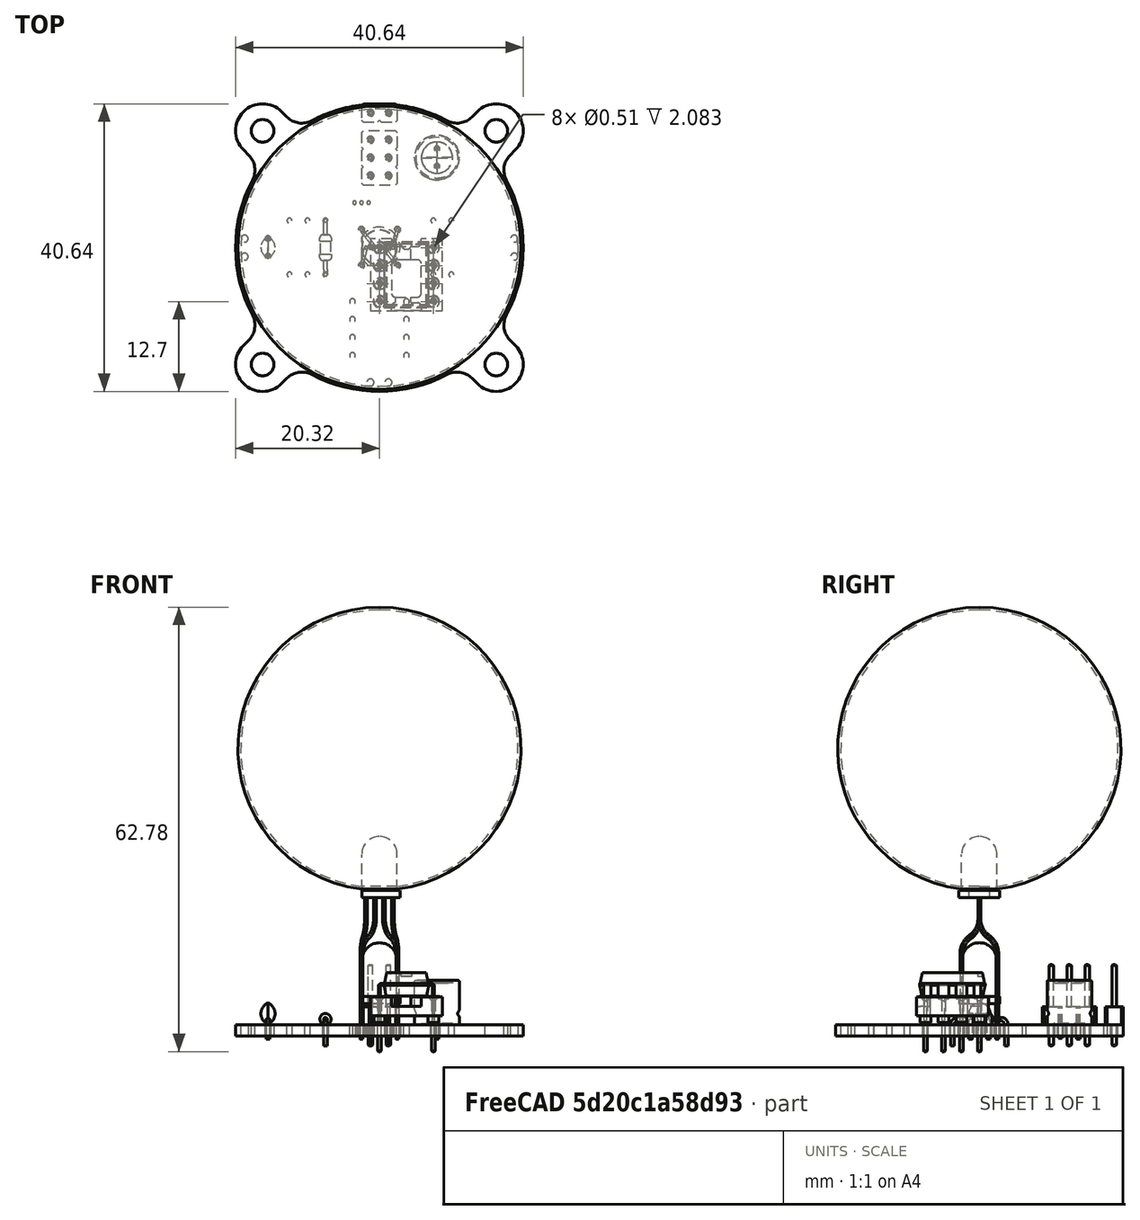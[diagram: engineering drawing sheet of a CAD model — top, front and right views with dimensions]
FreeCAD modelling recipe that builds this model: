
FCSTD DOCUMENT  (FreeCAD 2022.709R28846 (Git))
Label: firefly_v1_grid
License: All rights reserved
LicenseURL: http://en.wikipedia.org/wiki/All_rights_reserved
objects: Part::Feature×21, App::Link×7, App::Part×6, Sketcher::SketchObject×3, Part::FeaturePython×2, PartDesign::CoordinateSystem×1, PartDesign::Revolution×1, PartDesign::Pocket×1, PartDesign::Body×1
note: 32 computed .brp shape members not serialized (recipe doc carries the construction recipe); baked Part::Feature solids carry a one-line shape summary decoded from their .brp

FEATURE [PartDesign::CoordinateSystem] Local_CS_3165
  AttacherType = Attacher::AttachEngine3D
  AttachmentSupport = -> [X_Axis001]
  MapMode = 2
  Support = -> [X_Axis001]
  TreeRank = 0
FEATURE [Part::Feature] Pcb_3165
  Placement = pos=(-50.7999,50.8008,0) rot=(0,0,1;0rad)
  TreeRank = 0
  shape: bbox 40.64 x 40.64 x 1.6 mm, 75 faces (baked)
FEATURE [Sketcher::SketchObject] PCB_Sketch_3165
  ArcFitTolerance = 0
  FullyConstrained = false
  TreeRank = 0
  sketch-geometry (24):
    g0: LineSegment StartX=-19.2041 StartY=13.8159 StartZ=0 EndX=-18.465 EndY=13.0769 EndZ=0
    g1: LineSegment StartX=19.2041 StartY=13.8159 StartZ=0 EndX=18.465 EndY=13.0769 EndZ=0
    g2: LineSegment StartX=-13.0769 StartY=-18.465 StartZ=0 EndX=-13.8159 EndY=-19.2041 EndZ=0
    g3: LineSegment StartX=-18.465 StartY=-13.0769 StartZ=0 EndX=-19.2041 EndY=-13.8159 EndZ=0
    g4: LineSegment StartX=18.465 StartY=-13.0769 StartZ=0 EndX=19.2041 EndY=-13.8159 EndZ=0
    g5: LineSegment StartX=13.0769 StartY=-18.465 StartZ=0 EndX=13.8159 EndY=-19.2041 EndZ=0
    g6: LineSegment StartX=-13.8159 StartY=19.2041 StartZ=0 EndX=-13.0769 EndY=18.465 EndZ=0
    g7: LineSegment StartX=13.8159 StartY=19.2041 StartZ=0 EndX=13.0769 EndY=18.465 EndZ=0
    g8: ArcOfCircle CenterX=16.51 CenterY=-16.51 CenterZ=0 NormalX=0 NormalY=0 NormalZ=-1 AngleXU=2.35619 Radius=3.80999 StartAngle=0 EndAngle=3.14159
    g9: ArcOfCircle CenterX=-16.51 CenterY=-16.51 CenterZ=0 NormalX=0 NormalY=0 NormalZ=-1 AngleXU=-2.35619 Radius=3.80999 StartAngle=0 EndAngle=3.14159
    g10: ArcOfCircle CenterX=-10.9556 CenterY=20.5864 CenterZ=0 NormalX=0 NormalY=0 NormalZ=-1 AngleXU=-2.05985 Radius=3 StartAngle=0 EndAngle=1.27445
    g11: ArcOfCircle CenterX=20.5864 CenterY=10.9556 CenterZ=0 NormalX=0 NormalY=0 NormalZ=-1 AngleXU=-0.489056 Radius=3 StartAngle=0 EndAngle=1.27445
    g12: ArcOfCircle CenterX=-20.5864 CenterY=10.9556 CenterZ=0 NormalX=0 NormalY=0 NormalZ=-1 AngleXU=2.35619 Radius=3 StartAngle=0 EndAngle=1.27445
    g13: ArcOfCircle CenterX=1.9315e-06 CenterY=-1.81384e-07 CenterZ=0 NormalX=0 NormalY=0 NormalZ=-1 AngleXU=-0.489056 Radius=20.32 StartAngle=0 EndAngle=0.978112
    g14: ArcOfCircle CenterX=-20.5864 CenterY=-10.9556 CenterZ=0 NormalX=0 NormalY=0 NormalZ=-1 AngleXU=2.65254 Radius=3 StartAngle=0 EndAngle=1.27445
    g15: ArcOfCircle CenterX=-1.9315e-06 CenterY=-1.81384e-07 CenterZ=0 NormalX=0 NormalY=0 NormalZ=-1 AngleXU=2.65254 Radius=20.32 StartAngle=0 EndAngle=0.978112
    g16: ArcOfCircle CenterX=-16.51 CenterY=16.51 CenterZ=0 NormalX=0 NormalY=0 NormalZ=-1 AngleXU=-0.785398 Radius=3.81 StartAngle=0 EndAngle=3.14159
    g17: ArcOfCircle CenterX=0 CenterY=-1.20457e-06 CenterZ=0 NormalX=0 NormalY=0 NormalZ=-1 AngleXU=1.08174 Radius=20.32 StartAngle=0 EndAngle=0.978111
    g18: ArcOfCircle CenterX=16.51 CenterY=16.51 CenterZ=0 NormalX=0 NormalY=0 NormalZ=-1 AngleXU=0.785405 Radius=3.81 StartAngle=6.28318 EndAngle=9.42477
    g19: ArcOfCircle CenterX=10.9556 CenterY=20.5864 CenterZ=0 NormalX=0 NormalY=0 NormalZ=-1 AngleXU=-2.35619 Radius=3 StartAngle=0 EndAngle=1.27445
    g20: ArcOfCircle CenterX=10.9556 CenterY=-20.5864 CenterZ=0 NormalX=0 NormalY=0 NormalZ=-1 AngleXU=1.08174 Radius=3 StartAngle=0 EndAngle=1.27445
    g21: ArcOfCircle CenterX=0 CenterY=2.65843e-06 CenterZ=0 NormalX=0 NormalY=0 NormalZ=-1 AngleXU=-2.05985 Radius=20.32 StartAngle=0 EndAngle=0.978112
    g22: ArcOfCircle CenterX=20.5864 CenterY=-10.9556 CenterZ=0 NormalX=0 NormalY=0 NormalZ=-1 AngleXU=-0.785398 Radius=3 StartAngle=0 EndAngle=1.27445
    g23: ArcOfCircle CenterX=-10.9556 CenterY=-20.5864 CenterZ=0 NormalX=0 NormalY=0 NormalZ=-1 AngleXU=0.785399 Radius=3 StartAngle=0 EndAngle=1.27445
  constraints (24):
    c: Coincident(g3,g9)
    c: Coincident(g0,g16)
    c: Coincident(g3,g14)
    c: Coincident(g0,g12)
    c: Coincident(g13,g14)
    c: Coincident(g12,g13)
    c: Coincident(g2,g9)
    c: Coincident(g6,g16)
    c: Coincident(g2,g23)
    c: Coincident(g6,g10)
    c: Coincident(g21,g23)
    c: Coincident(g10,g17)
    c: Coincident(g20,g21)
    c: Coincident(g17,g19)
    c: Coincident(g5,g20)
    c: Coincident(g7,g19)
    c: Coincident(g5,g8)
    c: Coincident(g7,g18)
    c: Coincident(g15,g22)
    c: Coincident(g11,g15)
    c: Coincident(g4,g22)
    c: Coincident(g1,g11)
    c: Coincident(g4,g8)
    c: Coincident(g1,g18)
FEATURE [Part::Feature] Shape  label="R3_R_Axial_DIN0204_L36mm_D16mm_P762mm_Horizontal_c94ef6852790"
  Placement = pos=(-7.61992,-3.8092,0) rot=(0,0,1;1.5708rad)
  TreeRank = 0
  shape: bbox 1.732 x 8.285 x 4.666 mm, 17 faces (baked)
FEATURE [Part::Feature] Shape001  label="J6_PinHeader_1x02_P254mm_Vertical_1fb545e78c9a"
  Placement = pos=(1.27,19.05,0) rot=(0,0,-1;1.5708rad)
  TreeRank = 0
  shape: bbox 5.08 x 2.54 x 11.54 mm, 52 faces (baked)
FEATURE [Part::Feature] Shape002  label="J2_PinHeader_2x03_P254mm_Vertical_75255a230ba9"
  Placement = pos=(-1.26992,15.2408,0) rot=(0,0,1;0rad)
  TreeRank = 0
  shape: bbox 5.08 x 7.62 x 11.54 mm, 130 faces (baked)
FEATURE [App::Link] R3_R_Axial_DIN0204_L36mm_D16mm_P762mm_Horizontal_c94ef6852790_ln_  label="R1_R_Axial_DIN0204_L36mm_D16mm_P762mm_Horizontal_8458a7f7837b"
  AutoLinkLabel = false
  AutoPlacement = true
  LinkPlacement = pos=(7.62008,-3.8092,0) rot=(0,0,1;1.5708rad)
  LinkedObject = -> Shape
  Placement = pos=(7.62008,-3.8092,0) rot=(0,0,1;1.5708rad)
  SyncGroupVisibility = false
  TreeRank = 0
  _LinkVersion = 1
FEATURE [App::Link] R3_R_Axial_DIN0204_L36mm_D16mm_P762mm_Horizontal_c94ef6852790_ln_001  label="R2_R_Axial_DIN0204_L36mm_D16mm_P762mm_Horizontal_5ecdbd408406"
  AutoLinkLabel = false
  AutoPlacement = true
  LinkPlacement = pos=(10.1601,-3.8092,0) rot=(0,0,1;1.5708rad)
  LinkedObject = -> Shape
  Placement = pos=(10.1601,-3.8092,0) rot=(0,0,1;1.5708rad)
  SyncGroupVisibility = false
  TreeRank = 0
  _LinkVersion = 1
FEATURE [Part::Feature] Part__Feature  label="Sweep"
  Placement = pos=(0,0,18) rot=(0,0,1;0rad)
  TreeRank = 0
  shape: bbox 1.087 x 3.44 x 20 mm, 6 faces (baked)
FEATURE [Part::Feature] Part__Feature001  label="Sweep001"
  Placement = pos=(0,0,18) rot=(0,0,1;0rad)
  TreeRank = 0
  shape: bbox 2.544 x 3.312 x 20 mm, 6 faces (baked)
FEATURE [Part::Feature] Part__Feature002  label="Sweep002"
  Placement = pos=(0,0,18) rot=(0,0,1;0rad)
  TreeRank = 0
  shape: bbox 2.544 x 3.312 x 20 mm, 6 faces (baked)
FEATURE [Part::Feature] Part__Feature003  label="Sweep003"
  Placement = pos=(0,0,18) rot=(0,0,1;0rad)
  TreeRank = 0
  shape: bbox 1.087 x 3.44 x 20 mm, 6 faces (baked)
FEATURE [Part::Feature] Part__Feature004  label="Body"
  Placement = pos=(0,0,18) rot=(0,0,1;0rad)
  TreeRank = 0
  shape: bbox 5.4 x 5.8 x 8.6 mm, 6 faces (baked)
FEATURE [App::Part] Part  label="D1_Part_bb995b444e8d"
  ClaimAllChildren = false
  ExportMode = 1
  Group = -> [Part__Feature,Part__Feature001,Part__Feature002,Part__Feature003,Part__Feature004]
  Origin = -> Origin008
  Placement = pos=(8e-05,0.0008,0) rot=(0,0,1;0rad)
  TreeRank = 0
  _ExportChildren = -> [Part__Feature,Part__Feature001,Part__Feature002,Part__Feature003,Part__Feature004]
  _GroupVersion = 1
FEATURE [App::Link] J6_PinHeader_1x02_P254mm_Vertical_1fb545e78c9a_ln_  label="J3_PinHeader_1x02_P254mm_Vertical_b2013f4671be"
  AutoLinkLabel = false
  AutoPlacement = true
  LinkPlacement = pos=(19.0501,1.2708,0) rot=(0,0,1;0rad)
  LinkedObject = -> Shape001
  Placement = pos=(19.0501,1.2708,0) rot=(0,0,1;0rad)
  SyncGroupVisibility = false
  TreeRank = 0
  _LinkVersion = 1
FEATURE [App::Link] J6_PinHeader_1x02_P254mm_Vertical_1fb545e78c9a_ln_001  label="J5_PinHeader_1x02_P254mm_Vertical_84eae51975c3"
  AutoLinkLabel = false
  AutoPlacement = true
  LinkPlacement = pos=(1.27008,-19.0492,0) rot=(0,0,-1;1.5708rad)
  LinkedObject = -> Shape001
  Placement = pos=(1.27008,-19.0492,0) rot=(0,0,-1;1.5708rad)
  SyncGroupVisibility = false
  TreeRank = 0
  _LinkVersion = 1
FEATURE [Part::Feature] Shape003  label="C1_CP_Radial_D63mm_P250mm_7c2f516e95ce"
  Placement = pos=(8.12808,13.9708,0) rot=(0,0,-1;1.5708rad)
  TreeRank = 0
  shape: bbox 8.053 x 7.785 x 8.3 mm, 46 faces (baked)
FEATURE [Part::Feature] Part__Feature005  label="DIP_8_W762mm_Socket_sp"
  TreeRank = 0
  shape: bbox 10.16 x 10.16 x 7.787 mm, 128 faces (baked)
FEATURE [Part::Feature] Part__Feature006  label="DIP_8_W762mm_Socket_sp001"
  TreeRank = 0
  shape: bbox 7.874 x 9.27 x 6.98 mm, 148 faces (baked)
FEATURE [App::Part] DIP_8_W762mm_Socket_sp  label="U1_DIP_8_W762mm_Socket_sp002_69b93f21e8f7"
  ClaimAllChildren = false
  ExportMode = 1
  Group = -> [Part__Feature005,Part__Feature006]
  Origin = -> Origin009
  Placement = pos=(-3.80992,-7.6192,0) rot=(0,0,1;0rad)
  TreeRank = 0
  _ExportChildren = -> [Part__Feature005,Part__Feature006]
  _GroupVersion = 1
FEATURE [Part::Feature] Shape004  label="Q1_LED_D5.0mm_18f4e428e7b4"
  Placement = pos=(-1.26992,0.0008,0) rot=(0,0,1;0rad)
  TreeRank = 0
  shape: bbox 5.4 x 5.8 x 14.1 mm, 16 faces (baked)
FEATURE [App::Link] R3_R_Axial_DIN0204_L36mm_D16mm_P762mm_Horizontal_c94ef6852790_ln_002  label="R4_R_Axial_DIN0204_L36mm_D16mm_P762mm_Horizontal_9a7c57c7740b"
  AutoLinkLabel = false
  AutoPlacement = true
  LinkPlacement = pos=(-12.6999,-3.8092,0) rot=(0,0,1;1.5708rad)
  LinkedObject = -> Shape
  Placement = pos=(-12.6999,-3.8092,0) rot=(0,0,1;1.5708rad)
  SyncGroupVisibility = false
  TreeRank = 0
  _LinkVersion = 1
FEATURE [App::Link] R3_R_Axial_DIN0204_L36mm_D16mm_P762mm_Horizontal_c94ef6852790_ln_003  label="R5_R_Axial_DIN0204_L36mm_D16mm_P762mm_Horizontal_b3e8beb4090c"
  AutoLinkLabel = false
  AutoPlacement = true
  LinkPlacement = pos=(-10.16,-3.8092,0) rot=(0,0,1;1.5708rad)
  LinkedObject = -> Shape
  Placement = pos=(-10.16,-3.8092,0) rot=(0,0,1;1.5708rad)
  SyncGroupVisibility = false
  TreeRank = 0
  _LinkVersion = 1
FEATURE [Part::Feature] Shape005  label="C2_C_Disc_D30mm_W20mm_P250mm_075f2212bfdc"
  Placement = pos=(-15.7479,1.2708,0) rot=(0,0,-1;1.5708rad)
  TreeRank = 0
  shape: bbox 2 x 3 x 5.1 mm, 12 faces (baked)
FEATURE [App::Link] J6_PinHeader_1x02_P254mm_Vertical_1fb545e78c9a_ln_002  label="J4_PinHeader_1x02_P254mm_Vertical_479eb6cafd83"
  AutoLinkLabel = false
  AutoPlacement = true
  LinkPlacement = pos=(-19.0499,1.2708,0) rot=(0,0,1;0rad)
  LinkedObject = -> Shape001
  Placement = pos=(-19.0499,1.2708,0) rot=(0,0,1;0rad)
  SyncGroupVisibility = false
  TreeRank = 0
  _LinkVersion = 1
FEATURE [App::Part] Top_3165
  ClaimAllChildren = false
  ExportMode = 1
  Group = -> [Shape,Shape001,Shape002,R3_R_Axial_DIN0204_L36mm_D16mm_P762mm_Horizontal_c94ef6852790_ln_,R3_R_Axial_DIN0204_L36mm_D16mm_P762mm_Horizontal_c94ef6852790_ln_001,Part,J6_PinHeader_1x02_P254mm_Vertical_1fb545e78c9a_ln_,J6_PinHeader_1x02_P254mm_Vertical_1fb545e78c9a_ln_001,Shape003,DIP_8_W762mm_Socket_sp,Shape004,R3_R_Axial_DIN0204_L36mm_D16mm_P762mm_Horizontal_c94ef6852790_ln_002,+3 more]
  Origin = -> Origin003
  TreeRank = 0
  _ExportChildren = -> [Shape,Shape001,Shape002,R3_R_Axial_DIN0204_L36mm_D16mm_P762mm_Horizontal_c94ef6852790_ln_,R3_R_Axial_DIN0204_L36mm_D16mm_P762mm_Horizontal_c94ef6852790_ln_001,Part,J6_PinHeader_1x02_P254mm_Vertical_1fb545e78c9a_ln_,J6_PinHeader_1x02_P254mm_Vertical_1fb545e78c9a_ln_001,Shape003,DIP_8_W762mm_Socket_sp,Shape004,R3_R_Axial_DIN0204_L36mm_D16mm_P762mm_Horizontal_c94ef6852790_ln_002,+3 more]
  _GroupVersion = 1
FEATURE [App::Part] Step_Models_3165
  ClaimAllChildren = false
  ExportMode = 1
  Group = -> [Top_3165]
  Origin = -> Origin002
  TreeRank = 0
  _ExportChildren = -> [Top_3165]
  _GroupVersion = 1
FEATURE [Part::Feature] pads_area020001  label="topPads_3165"
  Placement = pos=(-50.7999,50.8008,0.02) rot=(0,0,1;0rad)
  TreeRank = 0
  shape: bbox 39.8 x 39.8 x 2e-07 mm, 49 faces, 0 solids (baked)
FEATURE [Part::Feature] Shape006001  label="topTracks_3165"
  Placement = pos=(-50.7999,50.8008,0.01) rot=(0,0,1;0rad)
  TreeRank = 0
  shape: bbox 38.35 x 37.13 x 2e-07 mm, 19 faces, 0 solids (baked)
FEATURE [Part::Feature] zones_area001  label="topZones_3165"
  Placement = pos=(-50.7999,50.8008,0.01) rot=(0,0,1;0rad)
  TreeRank = 0
  shape: bbox 40.4 x 40.4 x 2e-07 mm, 1 faces, 0 solids (baked)
FEATURE [Part::Feature] pads_area020022001  label="botPads_3165"
  Placement = pos=(-50.7999,50.8008,-1.62) rot=(0,0,1;0rad)
  TreeRank = 0
  shape: bbox 39.8 x 39.8 x 2e-07 mm, 49 faces, 0 solids (baked)
FEATURE [Part::Feature] Shape006002001  label="botTracks_3165"
  Placement = pos=(-50.7999,50.8008,-1.61) rot=(0,0,1;0rad)
  TreeRank = 0
  shape: bbox 38.35 x 37.13 x 2e-07 mm, 5 faces, 0 solids (baked)
FEATURE [Part::Feature] zones_area002001  label="botZones_3165"
  Placement = pos=(-50.7999,50.8008,-1.61) rot=(0,0,1;0rad)
  TreeRank = 0
  shape: bbox 40.4 x 40.4 x 2e-07 mm, 1 faces, 0 solids (baked)
FEATURE [Part::Feature] topSilks_3a64
  Placement = pos=(-50.7999,50.8008,0.07) rot=(0,0,1;0rad)
  TreeRank = 1
  shape: bbox 40.15 x 40.15 x 2e-07 mm, 56 faces, 0 solids (baked)
FEATURE [App::Part] Board_Geoms_3165
  ClaimAllChildren = false
  ExportMode = 1
  Group = -> [Pcb_3165,PCB_Sketch_3165,pads_area020001,Shape006001,zones_area001,pads_area020022001,Shape006002001,zones_area002001,topSilks_3a64]
  Origin = -> Origin
  TreeRank = 0
  _ExportChildren = -> [Pcb_3165,PCB_Sketch_3165,pads_area020001,Shape006001,zones_area001,pads_area020022001,Shape006002001,zones_area002001,topSilks_3a64]
  _GroupVersion = 1
FEATURE [App::Part] Board_3165  label="firefly"
  ClaimAllChildren = false
  ExportMode = 1
  Group = -> [Local_CS_3165,Board_Geoms_3165,Step_Models_3165]
  Origin = -> Origin001
  TreeRank = 11
  _ExportChildren = -> [Local_CS_3165,Board_Geoms_3165,Step_Models_3165]
  _GroupVersion = 1
FEATURE [Part::FeaturePython] Array  # Draft array (typed FeaturePython)
  AlwaysSyncPlacement = false
  Angle = 360
  ArrayType = 0
  AutoPlacement = true
  Axis = (0,0,1)
  Base = -> Board_3165
  BuildShape = true
  Center = (0,0,0)
  Count = 6
  ExpandArray = false
  Fuse = false
  IntervalAxis = (0,0,0)
  IntervalX = (40.64,0,0)
  IntervalY = (0,40.64,0)
  IntervalZ = (0,0,100)
  NumberCircles = 3
  NumberPolar = 5
  NumberX = 3
  NumberY = 2
  NumberZ = 1
  PlacementList = 6 placements: [(0,0,0),(0,40.64,0),(40.64,0,0),(40.64,40.64,0),(81.28,0,0),(81.28,40.64,0)]
  RadialDistance = 50
  ScaleList = (6) [(1,1,1),(1,1,1),(1,1,1),(1,1,1),(1,1,1),(1,1,1)]
  Symmetry = 1
  TangentialDistance = 25
  TreeRank = 12
  _LinkVersion = 0
FEATURE [Sketcher::SketchObject] Sketch
  ArcFitTolerance = 1e-06
  AttachmentSupport = -> [XZ_Plane010]
  FullyConstrained = true
  MapMode = 5
  Placement = pos=(0,0,0) rot=(1,0,0;1.5708rad)
  Support = -> [XZ_Plane010]
  TreeRank = 12
  sketch-geometry (4):
    g0: ArcOfCircle CenterX=0 CenterY=39 CenterZ=0 NormalX=0 NormalY=0 NormalZ=1 AngleXU=0 Radius=20 StartAngle=1.5708 EndAngle=4.71239
    g1: ArcOfCircle CenterX=0 CenterY=39 CenterZ=0 NormalX=0 NormalY=0 NormalZ=1 AngleXU=0 Radius=19.6 StartAngle=1.5708 EndAngle=4.71239
    g2: LineSegment StartX=0 StartY=59 StartZ=0 EndX=0 EndY=58.6 EndZ=0
    g3: LineSegment StartX=0 StartY=19 StartZ=0 EndX=0 EndY=19.4 EndZ=0
  constraints (13):
    c: PointOnObject(g0,g-2)
    c: PointOnObject(g0,g-2)
    c: Radius(g0) = 20
    c: Coincident(g1,g0)
    c: Coincident(g2,g0)
    c: Coincident(g2,g1)
    c: Vertical(g2)
    c: Coincident(g3,g0)
    c: Coincident(g3,g1)
    c: PointOnObject(g0,g-2)
    c: Vertical(g3)
    c: DistanceY(g2,g2) = 0.4
    c: DistanceY(g-1,g0) = 39
FEATURE [PartDesign::Revolution] Revolution
  Angle = 360
  Axis = (0,-2e-16,1)
  Base = (0,0,0)
  ClaimChildren = false
  Fit = 0
  FitJoin = 0
  InnerFit = 0
  InnerFitJoin = 0
  NewSolid = false
  Placement = pos=(0,0,0) rot=(1,0,0;1.5708rad)
  Profile = -> Sketch
  ReferenceAxis = -> Sketch [V_Axis]
  Suppress = false
  TreeRank = 13
  _ProfileBasedVersion = 1
FEATURE [Sketcher::SketchObject] Sketch001
  ArcFitTolerance = 1e-06
  FullyConstrained = true
  TreeRank = 14
  sketch-geometry (1):
    g0: Circle CenterX=0 CenterY=0 CenterZ=0 NormalX=0 NormalY=0 NormalZ=1 AngleXU=0 Radius=2.5
  constraints (2):
    c: Coincident(g0,g-1)
    c: Diameter(g0) = 5
FEATURE [PartDesign::Pocket] Pocket
  BaseFeature = -> Revolution
  ClaimChildren = false
  ColoredElements = -> Pocket [Face1,Face3]
  Fit = 0
  FitJoin = 0
  InnerFit = 0
  InnerFitJoin = 0
  InnerTaperAngle = 0
  InnerTaperAngleRev = 0
  Length = 20
  Length2 = 100
  Linearize = true
  NewSolid = false
  Placement = pos=(0,0,0) rot=(1,0,0;1.5708rad)
  Profile = -> Sketch001
  Reversed = true
  Suppress = false
  TreeRank = 15
  Type = 0
  _ProfileBasedVersion = 1
FEATURE [PartDesign::Body] Body  label="Body001"
  AutoGroupSolids = false
  ClaimAllChildren = false
  ExportMode = 0
  Group = -> [Sketch,Revolution,Sketch001,Pocket]
  Origin = -> Origin010
  Tip = -> Pocket
  TreeRank = 16
  _ExportChildren = -> [Revolution,Pocket]
  _GroupVersion = 1
FEATURE [Part::FeaturePython] Array001  # Draft array (typed FeaturePython)
  AlwaysSyncPlacement = false
  Angle = 360
  ArrayType = 0
  AutoPlacement = true
  Axis = (0,0,1)
  Base = -> Body
  BuildShape = true
  Center = (0,0,0)
  Count = 6
  ExpandArray = false
  Fuse = false
  IntervalAxis = (0,0,0)
  IntervalX = (40.64,0,0)
  IntervalY = (0,40.64,0)
  IntervalZ = (0,0,100)
  NumberCircles = 3
  NumberPolar = 5
  NumberX = 3
  NumberY = 2
  NumberZ = 1
  PlacementList = 6 placements: [(0,0,0),(0,40.64,0),(40.64,0,0),(40.64,40.64,0),(81.28,0,0),(81.28,40.64,0)]
  RadialDistance = 50
  ScaleList = (6) [(1,1,1),(1,1,1),(1,1,1),(1,1,1),(1,1,1),(1,1,1)]
  Symmetry = 1
  TangentialDistance = 25
  TreeRank = 17
  _LinkVersion = 0
